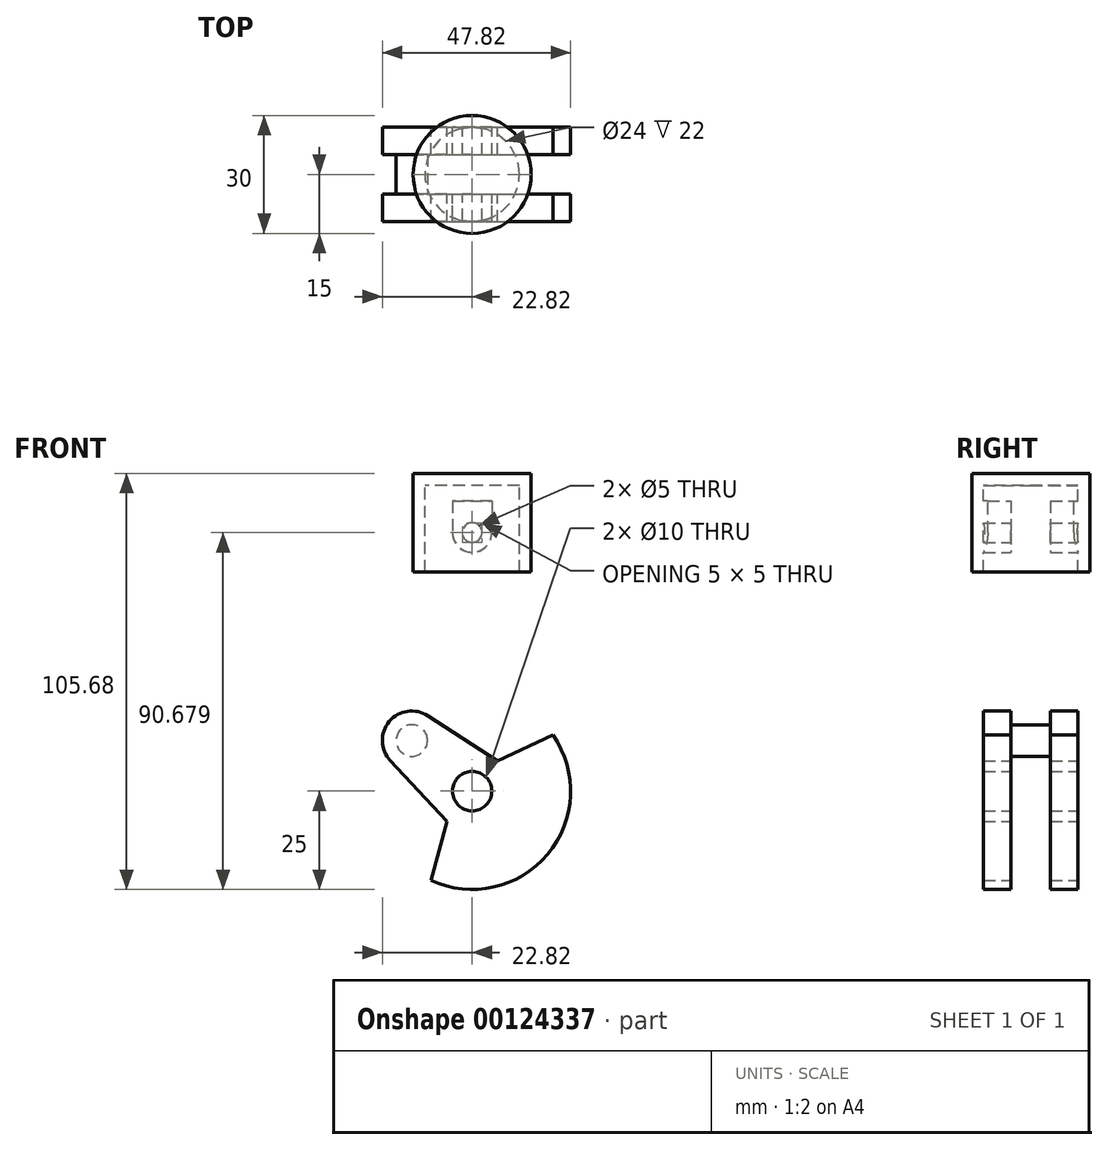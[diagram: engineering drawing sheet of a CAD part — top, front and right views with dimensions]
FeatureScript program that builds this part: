
annotation { "Feature Type Name" : "Feature", "Feature Type Description" : "" }
export const myFeature = defineFeature(function(context is Context, id is Id, definition is map)
    precondition{}
    {
        {
            var Q0;
            Q0=qCreatedBy(makeId("Front.planeOp"),FACE);
            var sketch = newSketch(context, id + "F0", { "sketchPlane" : qUnion([Q0])});
            skLineSegment(sketch, "E0", {"start": v(-57.38, 0) * mm, "end": v(57.64, 0) * mm, "construction": true});
            skLineSegment(sketch, "E1", {"start": v(-57.38, 50) * mm, "end": v(52.76, 50) * mm, "construction": true});
            skLineSegment(sketch, "E2", {"start": v(-2.3, 50) * mm, "end": v(-2.3, 50) * mm});
            skLineSegment(sketch, "E3", {"start": v(-90.13, 80) * mm, "end": v(58.33, 80) * mm, "construction": true});
            skLineSegment(sketch, "E4", {"start": v(0, 0) * mm, "end": v(-15.32, 12.86) * mm});
            skLineSegment(sketch, "E5", {"start": v(0, 80) * mm, "end": v(0, -103.57) * mm, "construction": true});
            skLineSegment(sketch, "E6.top", {"start": v(-15, 80.68) * mm, "end": v(15, 80.68) * mm});
            skLineSegment(sketch, "E7", {"start": v(0, 65.68) * mm, "end": v(-15.32, 12.86) * mm});
            skLineSegment(sketch, "E8.bottom", {"start": v(-5, 80.68) * mm, "end": v(5, 80.68) * mm});
            skLineSegment(sketch, "E8.top", {"start": v(-5, 73.68) * mm, "end": v(5, 73.68) * mm});
            skLineSegment(sketch, "E8.left", {"start": v(-5, 80.68) * mm, "end": v(-5, 73.68) * mm});
            skLineSegment(sketch, "E8.right", {"start": v(5, 80.68) * mm, "end": v(5, 73.68) * mm});
            skLineSegment(sketch, "E9", {"start": v(5, 73.68) * mm, "end": v(5, 65.68) * mm});
            skCircle(sketch, "E10", {"center": v(0, 65.68) * mm, "radius": 2.5 * mm});
            skLineSegment(sketch, "E11", {"start": v(-5, 73.68) * mm, "end": v(-5, 65.68) * mm});
            skArc(sketch, "E12", {"start": v(-5, 65.68) * mm, "mid": v(0, 60.68) * mm, "end": v(5, 65.68) * mm});
            skLineSegment(sketch, "E13", {"start": v(-15, 80.68) * mm, "end": v(-15, 55.68) * mm});
            skLineSegment(sketch, "E14", {"start": v(-15, 55.68) * mm, "end": v(15, 55.68) * mm});
            skLineSegment(sketch, "E15", {"start": v(15, 55.68) * mm, "end": v(15, 80.68) * mm});
            skSolve(sketch);
        }
        {
            var Q0;
            Q0=qCreatedBy(makeId("Front.planeOp"),FACE);
            var sketch = newSketch(context, id + "F1", { "sketchPlane" : qUnion([Q0])});
            skCircle(sketch, "E16", {"center": v(-15.32, 12.86) * mm, "radius": 7.5 * mm});
            skLineSegment(sketch, "E17", {"start": v(-20.8, 7.74) * mm, "end": v(-6.43, -7.66) * mm});
            skLineSegment(sketch, "E18", {"start": v(-11.23, 19.14) * mm, "end": v(6.43, 7.66) * mm});
            skLineSegment(sketch, "E19", {"start": v(-15.32, 12.86) * mm, "end": v(0, 0) * mm, "construction": true});
            skLineSegment(sketch, "E20", {"start": v(-6.43, -7.66) * mm, "end": v(6.43, 7.66) * mm, "construction": true});
            skCircle(sketch, "E21", {"center": v(0, 0) * mm, "radius": 10 * mm});
            skCircle(sketch, "E22", {"center": v(0, 0) * mm, "radius": 5 * mm});
            skLineSegment(sketch, "E23", {"start": v(0, 0) * mm, "end": v(19.15, -16.07) * mm, "construction": true});
            skLineSegment(sketch, "E24", {"start": v(6.43, 7.66) * mm, "end": v(20.55, 14.24) * mm});
            skLineSegment(sketch, "E25", {"start": v(-6.43, -7.66) * mm, "end": v(-10.46, -22.7) * mm});
            skArc(sketch, "E26", {"start": v(-10.46, -22.7) * mm, "mid": v(19.15, -16.07) * mm, "end": v(20.55, 14.24) * mm});
            skCircle(sketch, "E27", {"center": v(-15.32, 12.86) * mm, "radius": 4 * mm});
            skSolve(sketch);
        }
        {
            var Q0;
            Q0=qCreatedBy(makeId("Front.planeOp"),FACE);
            var sketch = newSketch(context, id + "F2", { "sketchPlane" : qUnion([Q0])});
            skLineSegment(sketch, "E28.0", {"start": v(0, 80.68) * mm, "end": v(15, 80.68) * mm});
            skLineSegment(sketch, "E29.0", {"start": v(0, 55.68) * mm, "end": v(15, 55.68) * mm});
            skLineSegment(sketch, "E30.0", {"start": v(15, 55.68) * mm, "end": v(15, 80.68) * mm});
            skLineSegment(sketch, "E31", {"start": v(0, 55.68) * mm, "end": v(0, 80.68) * mm});
            skPoint(sketch, "E32.orphan", {"position": v(-15, 80.68) * mm});
            skPoint(sketch, "E33.orphan", {"position": v(-15, 55.68) * mm});
            skSolve(sketch);
        }
        {
            var Q0;
            Q0=makeQuery(id+"F2.imprint","IMPRINT",FACE,{"disambiguationData":[TD([[makeQuery(id+"F2.imprint","IMPRINT",EDGE,{"derivedFrom":sQuery(id+"F2.wireOp",EDGE,"E28.0")}),-1.0]])]});
            var Q1;
            Q1=sQuery(id+"F0.wireOp",EDGE,"E5");
            revolve(context, id + "F3", {"entities" : qUnion([Q0]), "axis" : qUnion([Q1]), "revolveType" : RevolveType.FULL});
        }
        {
            var Q0;
            Q0=makeQuery(id+"F3.opRevolve","SWEPT_FACE",FACE,{"disambiguationData":[OSD([sQuery(id+"F2.wireOp",EDGE,"E29.0")])]});
            shell(context, id + "F4", {"entities" : qUnion([Q0]), "thickness" : 3 * mm});
        }
        {
            var Q0;
            Q0=makeQuery(id+"F0.imprint","IMPRINT",FACE,{"disambiguationData":[TD([[makeQuery(id+"F0.imprint","IMPRINT",EDGE,{"derivedFrom":sQuery(id+"F0.wireOp",EDGE,"E8.bottom")}),-1.0]])]});
            var Q1;
            Q1=makeQuery(id+"F0.imprint","IMPRINT",FACE,{"disambiguationData":[TD([[makeQuery(id+"F0.imprint","IMPRINT",EDGE,{"derivedFrom":sQuery(id+"F0.wireOp",EDGE,"E8.top")}),-1.0]])]});
            var Q2;
            Q2=makeQuery(id+"F4.opShell","OFFSET_FACE",FACE,{"disambiguationData":[OSD([sQuery(id+"F2.wireOp",EDGE,"E30.0")])]});
            var Q3;
            Q3=makeQuery(id+"F4.opShell","OFFSET_FACE",FACE,{"disambiguationData":[OSD([sQuery(id+"F2.wireOp",EDGE,"E30.0")])]});
            extrude(context, id + "F5", {"entities" : qUnion([Q0, Q1]), "operationType" : NewBodyOperationType.ADD, "endBound" : BoundingType.UP_TO_SURFACE, "endBoundEntityFace" : qUnion([Q2]), "depth" : 25 * mm, "hasSecondDirection" : true, "secondDirectionBound" : SecondDirectionBoundingType.UP_TO_SURFACE, "secondDirectionOppositeDirection" : true, "secondDirectionBoundEntityFace" : qUnion([Q3]), "secondDirectionDepth" : 25 * mm});
        }
        {
            var Q0;
            {var subQ2=sQuery(id+"F1.wireOp",EDGE,"E24");Q0=makeQuery(id+"F1.imprint","IMPRINT",FACE,{"disambiguationData":[TD([[makeQuery(id+"F1.imprint","IMPRINT",EDGE,{"derivedFrom":subQ2}),-1.0]])]});}
            var Q1;
            Q1=makeQuery(id+"F1.imprint","IMPRINT",FACE,{"disambiguationData":[TD([[makeQuery(id+"F1.imprint","IMPRINT",EDGE,{"derivedFrom":sQuery(id+"F1.wireOp",EDGE,"E22")}),-1.0]])]});
            var Q2;
            {var subQ0=sQuery(id+"F1.wireOp",EDGE,"E17");var subQ1=sQuery(id+"F1.wireOp",EDGE,"E16");var subQ2=makeQuery(id+"F1.imprint","INTERSECT",VERTEX,{"derivedFrom":[subQ1,subQ0]});Q2=makeQuery(id+"F1.imprint","IMPRINT",FACE,{"disambiguationData":[TD([[makeQuery(id+"F1.imprint","IMPRINT",EDGE,{"disambiguationData":[TD([[subQ2,-1.0]])],"derivedFrom":subQ1}),-1.0]])]});}
            var Q3;
            {var subQ0=sQuery(id+"F1.wireOp",EDGE,"E16");var subQ1=makeQuery(id+"F1.imprint","INTERSECT",VERTEX,{"derivedFrom":[subQ0,sQuery(id+"F1.wireOp",EDGE,"E17")]});Q3=makeQuery(id+"F1.imprint","IMPRINT",FACE,{"disambiguationData":[TD([[makeQuery(id+"F1.imprint","IMPRINT",EDGE,{"disambiguationData":[TD([[subQ1,1.0]])],"derivedFrom":subQ0}),1.0]])]});}
            extrude(context, id + "F6", {"entities" : qUnion([Q0, Q1, Q2, Q3]), "depth" : 12 * mm, "hasSecondDirection" : true, "secondDirectionOppositeDirection" : true, "secondDirectionDepth" : 12 * mm});
        }
        {
            var Q0;
            Q0=makeQuery(id+"F1.imprint","IMPRINT",FACE,{"disambiguationData":[TD([[makeQuery(id+"F1.imprint","IMPRINT",EDGE,{"derivedFrom":sQuery(id+"F1.wireOp",EDGE,"E27")}),1.0]])]});
            extrude(context, id + "F7", {"entities" : qUnion([Q0]), "operationType" : NewBodyOperationType.ADD, "endBound" : BoundingType.SYMMETRIC, "depth" : 24 * mm});
        }
        {
            var Q0;
            Q0=makeQuery(id+"F0.imprint","IMPRINT",FACE,{"disambiguationData":[TD([[makeQuery(id+"F0.imprint","IMPRINT",EDGE,{"derivedFrom":sQuery(id+"F0.wireOp",EDGE,"E8.top")}),-1.0]])]});
            extrude(context, id + "F8", {"entities" : qUnion([Q0]), "operationType" : NewBodyOperationType.REMOVE, "endBound" : BoundingType.SYMMETRIC, "oppositeDirection" : true, "depth" : 10 * mm});
        }
        {
            var Q0;
            {var subQ2=sQuery(id+"F1.wireOp",EDGE,"E24");Q0=makeQuery(id+"F1.imprint","IMPRINT",FACE,{"disambiguationData":[TD([[makeQuery(id+"F1.imprint","IMPRINT",EDGE,{"derivedFrom":subQ2}),-1.0]])]});}
            var Q1;
            {var subQ0=sQuery(id+"F1.wireOp",EDGE,"E17");var subQ1=sQuery(id+"F1.wireOp",EDGE,"E16");var subQ2=makeQuery(id+"F1.imprint","INTERSECT",VERTEX,{"derivedFrom":[subQ1,subQ0]});Q1=makeQuery(id+"F1.imprint","IMPRINT",FACE,{"disambiguationData":[TD([[makeQuery(id+"F1.imprint","IMPRINT",EDGE,{"disambiguationData":[TD([[subQ2,-1.0]])],"derivedFrom":subQ1}),-1.0]])]});}
            var Q2;
            Q2=makeQuery(id+"F1.imprint","IMPRINT",FACE,{"disambiguationData":[TD([[makeQuery(id+"F1.imprint","IMPRINT",EDGE,{"derivedFrom":sQuery(id+"F1.wireOp",EDGE,"E27")}),-1.0]])]});
            var Q3;
            Q3=makeQuery(id+"F1.imprint","IMPRINT",FACE,{"disambiguationData":[TD([[makeQuery(id+"F1.imprint","IMPRINT",EDGE,{"derivedFrom":sQuery(id+"F1.wireOp",EDGE,"E22")}),-1.0]])]});
            extrude(context, id + "F9", {"entities" : qUnion([Q0, Q1, Q2, Q3]), "operationType" : NewBodyOperationType.REMOVE, "endBound" : BoundingType.SYMMETRIC, "oppositeDirection" : true, "depth" : 10 * mm});
        }
    });
